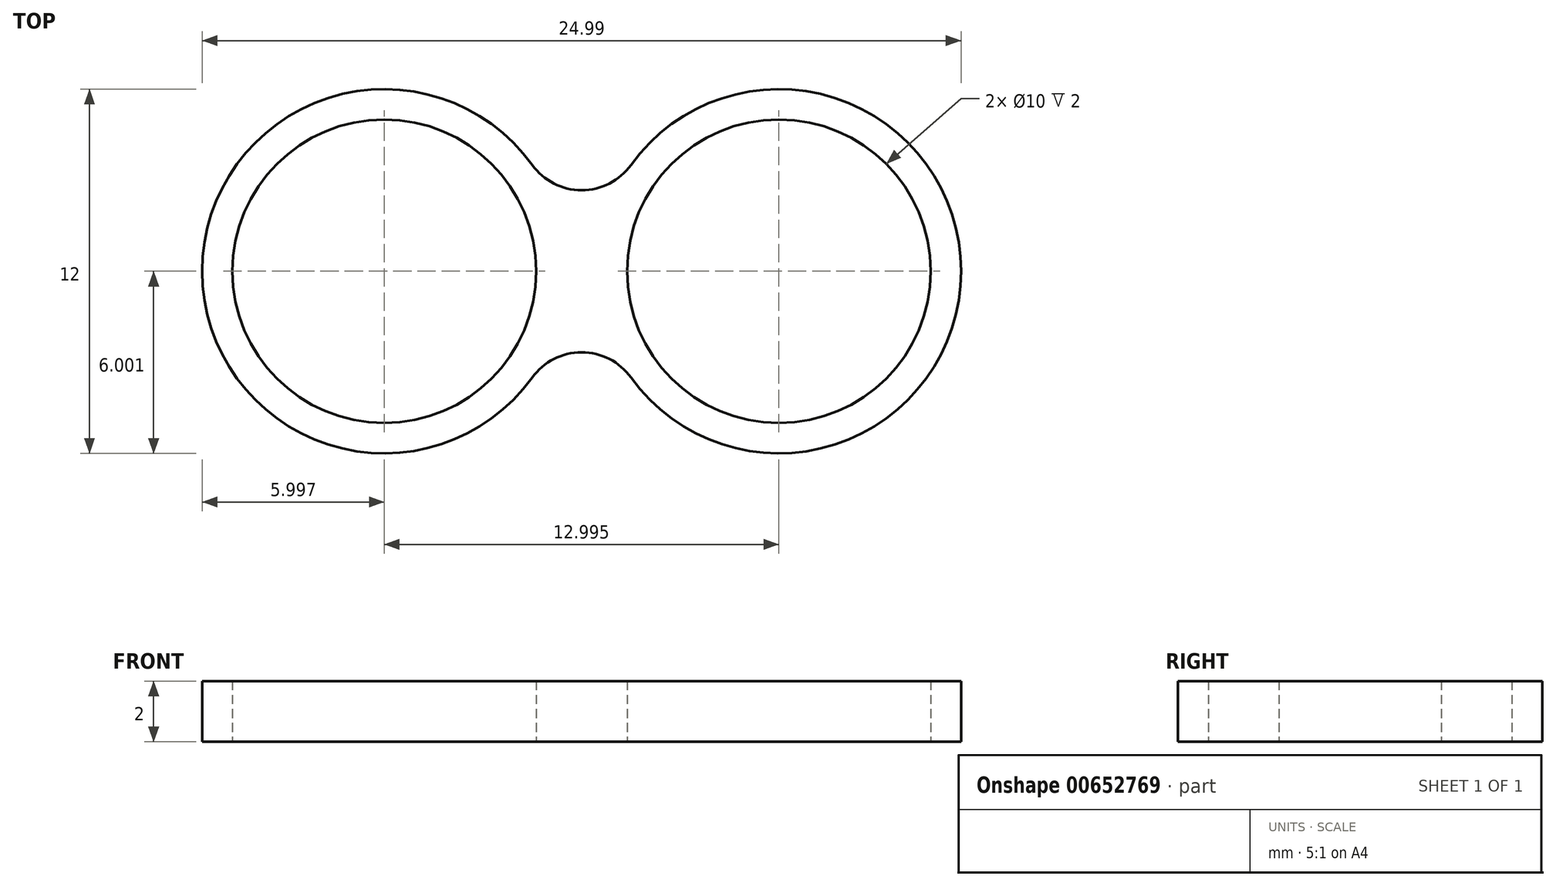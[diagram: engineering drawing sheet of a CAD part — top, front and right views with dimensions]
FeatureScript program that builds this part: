
annotation { "Feature Type Name" : "Feature", "Feature Type Description" : "" }
export const myFeature = defineFeature(function(context is Context, id is Id, definition is map)
    precondition{}
    {
        {
            var Q0;
            Q0=qCreatedBy(makeId("Top.planeOp"),FACE);
            var sketch = newSketch(context, id + "F0", { "sketchPlane" : qUnion([Q0])});
            skCircle(sketch, "E0", {"center": v(-12.87, 5.8) * mm, "radius": 5 * mm});
            skArc(sketch, "E1", {"start": v(-8, 9.3) * mm, "mid": v(-18.87, 5.8) * mm, "end": v(-8, 2.3) * mm});
            skLineSegment(sketch, "E2", {"start": v(-12.87, 5.8) * mm, "end": v(19.31, 5.8) * mm, "construction": true});
            skLineSegment(sketch, "E3", {"start": v(-7.5, 15.7) * mm, "end": v(-7.5, -8.18) * mm, "construction": true});
            skLineSegment(sketch, "E4", {"start": v(-6.38, 15.64) * mm, "end": v(-6.38, -5.35) * mm, "construction": true});
            skArc(sketch, "E5.MirrorCS", {"start": v(-4.75, 9.3) * mm, "mid": v(6.12, 5.8) * mm, "end": v(-4.75, 2.3) * mm});
            skCircle(sketch, "E6.MirrorC", {"center": v(0.12, 5.8) * mm, "radius": 5 * mm});
            skLineSegment(sketch, "E7", {"start": v(-6.38, 3.13) * mm, "end": v(-6.37, 3.13) * mm});
            skLineSegment(sketch, "E8", {"start": v(-6.38, 8.47) * mm, "end": v(-6.37, 8.47) * mm});
            skPoint(sketch, "E9.visualSharp", {"position": v(-7.5, 8.47) * mm});
            skArc(sketch, "E9.filletArc", {"start": v(-8, 9.3) * mm, "mid": v(-7.3, 8.7) * mm, "end": v(-6.38, 8.47) * mm});
            skPoint(sketch, "E10.visualSharp", {"position": v(-5.25, 8.47) * mm});
            skArc(sketch, "E10.filletArc", {"start": v(-6.37, 8.47) * mm, "mid": v(-5.46, 8.7) * mm, "end": v(-4.75, 9.3) * mm});
            skPoint(sketch, "E11.visualSharp", {"position": v(-7.5, 3.13) * mm});
            skArc(sketch, "E11.filletArc", {"start": v(-6.38, 3.13) * mm, "mid": v(-7.3, 2.91) * mm, "end": v(-8, 2.3) * mm});
            skPoint(sketch, "E12.visualSharp", {"position": v(-5.25, 3.13) * mm});
            skArc(sketch, "E12.filletArc", {"start": v(-4.75, 2.3) * mm, "mid": v(-5.46, 2.91) * mm, "end": v(-6.37, 3.13) * mm});
            skSolve(sketch);
        }
        {
            var Q0;
            Q0=makeQuery(id+"F0.imprint","IMPRINT",FACE,{"disambiguationData":[TD([[makeQuery(id+"F0.imprint","IMPRINT",EDGE,{"derivedFrom":sQuery(id+"F0.wireOp",EDGE,"E0")}),-1.0]])]});
            extrude(context, id + "F1", {"entities" : qUnion([Q0]), "depth" : 2 * mm, "offsetDistance" : 25 * mm});
        }
    });
